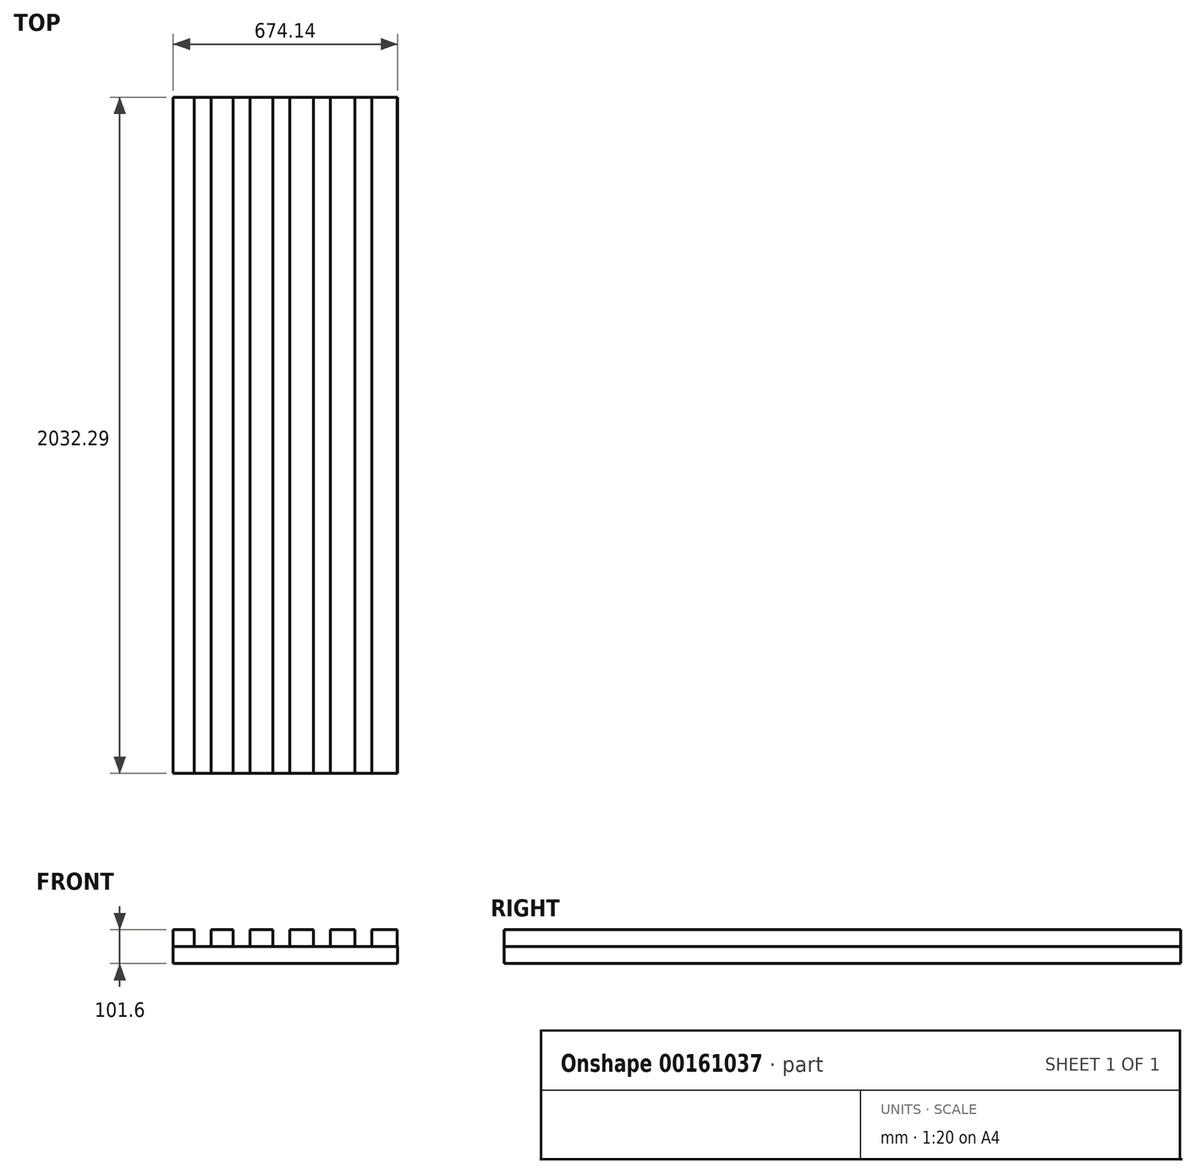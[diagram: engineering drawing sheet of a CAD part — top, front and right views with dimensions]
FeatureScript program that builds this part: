
annotation { "Feature Type Name" : "Feature", "Feature Type Description" : "" }
export const myFeature = defineFeature(function(context is Context, id is Id, definition is map)
    precondition{}
    {
        {
            var Q0;
            Q0=qCreatedBy(makeId("Top.planeOp"),FACE);
            var sketch = newSketch(context, id + "F0", { "sketchPlane" : qUnion([Q0])});
            skLineSegment(sketch, "E0.bottom", {"start": v(0, 0) * mm, "end": v(63.5, 0) * mm});
            skLineSegment(sketch, "E0.top", {"start": v(0, 2032) * mm, "end": v(63.5, 2032) * mm});
            skLineSegment(sketch, "E0.left", {"start": v(0, 0) * mm, "end": v(0, 2032) * mm});
            skLineSegment(sketch, "E0.right", {"start": v(63.5, 0) * mm, "end": v(63.5, 2032) * mm});
            skLineSegment(sketch, "E1", {"start": v(63.5, 2032) * mm, "end": v(114.3, 2032) * mm});
            skLineSegment(sketch, "E2.bottom", {"start": v(114.3, 2032) * mm, "end": v(180.34, 2032) * mm});
            skLineSegment(sketch, "E2.top", {"start": v(114.3, 0) * mm, "end": v(180.34, 0) * mm});
            skLineSegment(sketch, "E2.left", {"start": v(114.3, 2032) * mm, "end": v(114.3, 0) * mm});
            skLineSegment(sketch, "E2.right", {"start": v(180.34, 2032) * mm, "end": v(180.34, 0) * mm});
            skLineSegment(sketch, "E3", {"start": v(180.34, 2032) * mm, "end": v(231.14, 2032) * mm});
            skLineSegment(sketch, "E4.bottom", {"start": v(231.14, 2032) * mm, "end": v(299.72, 2032) * mm});
            skLineSegment(sketch, "E4.top", {"start": v(231.14, 0) * mm, "end": v(299.72, 0) * mm});
            skLineSegment(sketch, "E4.left", {"start": v(231.14, 2032) * mm, "end": v(231.14, 0) * mm});
            skLineSegment(sketch, "E4.right", {"start": v(299.72, 2032) * mm, "end": v(299.72, 0) * mm});
            skLineSegment(sketch, "E5", {"start": v(299.72, 2032) * mm, "end": v(350.52, 2032) * mm});
            skLineSegment(sketch, "E6.bottom", {"start": v(350.52, 2032) * mm, "end": v(421.64, 2032) * mm});
            skLineSegment(sketch, "E6.top", {"start": v(350.52, 0) * mm, "end": v(421.64, 0) * mm});
            skLineSegment(sketch, "E6.left", {"start": v(350.52, 2032) * mm, "end": v(350.52, 0) * mm});
            skLineSegment(sketch, "E6.right", {"start": v(421.64, 2032) * mm, "end": v(421.64, 0) * mm});
            skLineSegment(sketch, "E7", {"start": v(421.64, 2032) * mm, "end": v(472.44, 2032) * mm});
            skLineSegment(sketch, "E8.bottom", {"start": v(472.44, 2032) * mm, "end": v(546.1, 2032) * mm});
            skLineSegment(sketch, "E8.top", {"start": v(472.44, 0) * mm, "end": v(546.1, 0) * mm});
            skLineSegment(sketch, "E8.left", {"start": v(472.44, 2032) * mm, "end": v(472.44, 0) * mm});
            skLineSegment(sketch, "E8.right", {"start": v(546.1, 2032) * mm, "end": v(546.1, 0) * mm});
            skLineSegment(sketch, "E9", {"start": v(546.1, 2032) * mm, "end": v(596.9, 2032) * mm});
            skLineSegment(sketch, "E10.bottom", {"start": v(596.9, 2032) * mm, "end": v(673.1, 2032) * mm});
            skLineSegment(sketch, "E10.top", {"start": v(596.9, 0) * mm, "end": v(673.1, 0) * mm});
            skLineSegment(sketch, "E10.left", {"start": v(596.9, 2032) * mm, "end": v(596.9, 0) * mm});
            skLineSegment(sketch, "E10.right", {"start": v(673.1, 2032) * mm, "end": v(673.1, 0) * mm});
            skSolve(sketch);
        }
        {
            var Q0;
            Q0 = qSketchRegion(id + "F0", true);
            extrude(context, id + "F1", {"entities" : qUnion([Q0]), "depth" : 50.8 * mm});
        }
        {
            var Q0;
            Q0=qCreatedBy(makeId("Top.planeOp"),FACE);
            var sketch = newSketch(context, id + "F2", { "sketchPlane" : qUnion([Q0])});
            skLineSegment(sketch, "E11.bottom", {"start": v(674.14, 0) * mm, "end": v(0, 0) * mm});
            skLineSegment(sketch, "E11.top", {"start": v(674.14, 2032.3) * mm, "end": v(0, 2032.3) * mm});
            skLineSegment(sketch, "E11.left", {"start": v(674.14, 0) * mm, "end": v(674.14, 2032.3) * mm});
            skLineSegment(sketch, "E11.right", {"start": v(0, 0) * mm, "end": v(0, 2032.3) * mm});
            skSolve(sketch);
        }
        {
            var Q0;
            Q0 = qSketchRegion(id + "F2", true);
            extrude(context, id + "F3", {"entities" : qUnion([Q0]), "oppositeDirection" : true, "depth" : 50.8 * mm});
        }
    });
